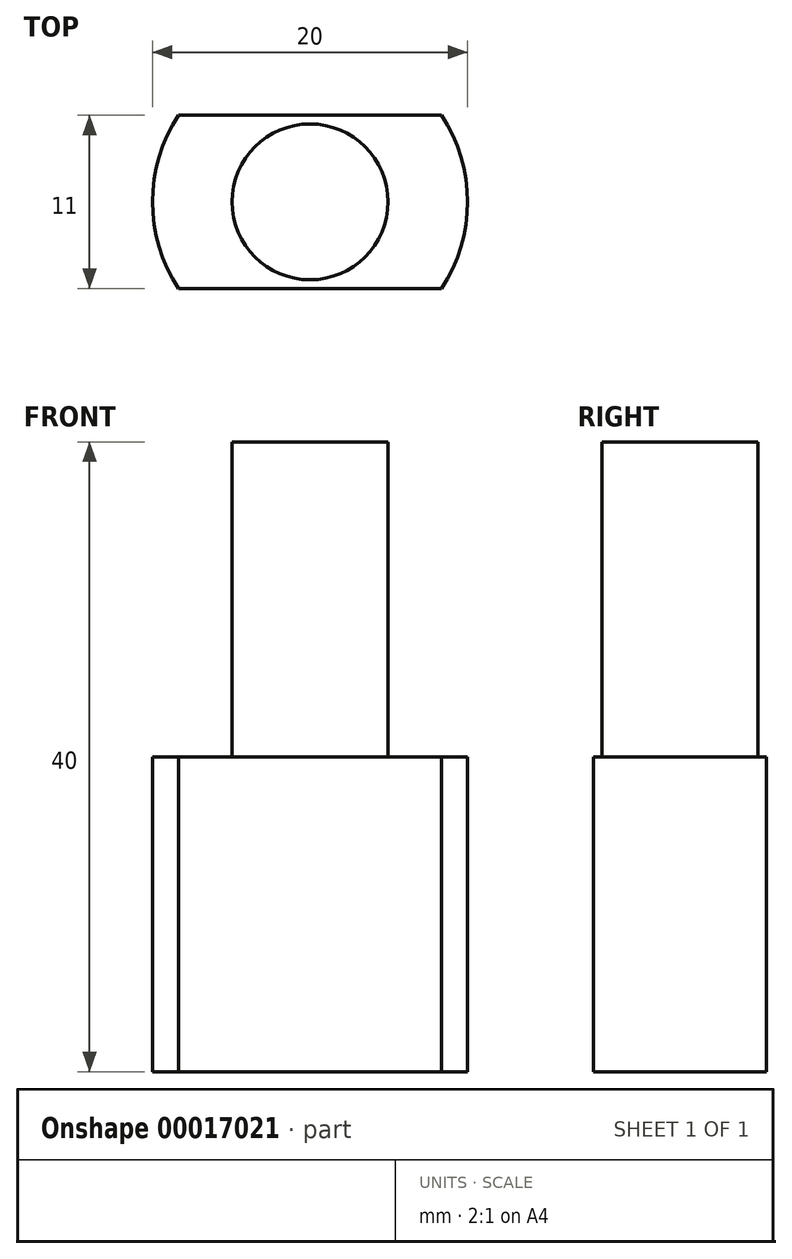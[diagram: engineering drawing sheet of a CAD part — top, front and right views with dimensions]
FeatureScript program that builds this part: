
annotation { "Feature Type Name" : "Feature", "Feature Type Description" : "" }
export const myFeature = defineFeature(function(context is Context, id is Id, definition is map)
    precondition{}
    {
        {
            var Q0;
            Q0=qCreatedBy(makeId("Top.planeOp"),FACE);
            var sketch = newSketch(context, id + "F0", { "sketchPlane" : qUnion([Q0])});
            skCircle(sketch, "E0", {"center": v(0, 0) * mm, "radius": 10 * mm});
            skSolve(sketch);
        }
        {
            var Q0;
            Q0 = qSketchRegion(id + "F0", true);
            extrude(context, id + "F1", {"entities" : qUnion([Q0]), "depth" : 20 * mm});
        }
        {
            var Q0;
            Q0=makeQuery(id+"F1.opExtrude","CAP_FACE",FACE,{"disambiguationData":[OSD([sQuery(id+"F0.wireOp",EDGE,"E0")])],"isStart":false});
            var sketch = newSketch(context, id + "F2", { "sketchPlane" : qUnion([Q0])});
            skCircle(sketch, "E1", {"center": v(0, 0) * mm, "radius": 4.95 * mm});
            skSolve(sketch);
        }
        {
            var Q0;
            Q0 = qSketchRegion(id + "F2", true);
            extrude(context, id + "F3", {"entities" : qUnion([Q0]), "operationType" : NewBodyOperationType.ADD, "depth" : 20 * mm});
        }
        {
            var Q0;
            Q0=makeQuery(id+"F1.opExtrude","CAP_FACE",FACE,{"disambiguationData":[OSD([sQuery(id+"F0.wireOp",EDGE,"E0")])],"isStart":true});
            var sketch = newSketch(context, id + "F4", { "sketchPlane" : qUnion([Q0])});
            skLineSegment(sketch, "E2.bottom", {"start": v(14.83, 5.5) * mm, "end": v(-13.02, 5.5) * mm});
            skLineSegment(sketch, "E2.top", {"start": v(14.83, 16.99) * mm, "end": v(-13.02, 16.99) * mm});
            skLineSegment(sketch, "E2.left", {"start": v(14.83, 5.5) * mm, "end": v(14.83, 16.99) * mm});
            skLineSegment(sketch, "E2.right", {"start": v(-13.02, 5.5) * mm, "end": v(-13.02, 16.99) * mm});
            skLineSegment(sketch, "E3.bottom", {"start": v(14.83, -16.99) * mm, "end": v(-13.02, -16.99) * mm});
            skLineSegment(sketch, "E3.top", {"start": v(14.83, -5.5) * mm, "end": v(-13.02, -5.5) * mm});
            skLineSegment(sketch, "E3.left", {"start": v(14.83, -16.99) * mm, "end": v(14.83, -5.5) * mm});
            skLineSegment(sketch, "E3.right", {"start": v(-13.02, -16.99) * mm, "end": v(-13.02, -5.5) * mm});
            skSolve(sketch);
        }
        {
            var Q0;
            Q0 = qSketchRegion(id + "F4", true);
            extrude(context, id + "F5", {"entities" : qUnion([Q0]), "operationType" : NewBodyOperationType.REMOVE, "endBound" : BoundingType.THROUGH_ALL, "oppositeDirection" : true, "depth" : 25 * mm});
        }
    });
